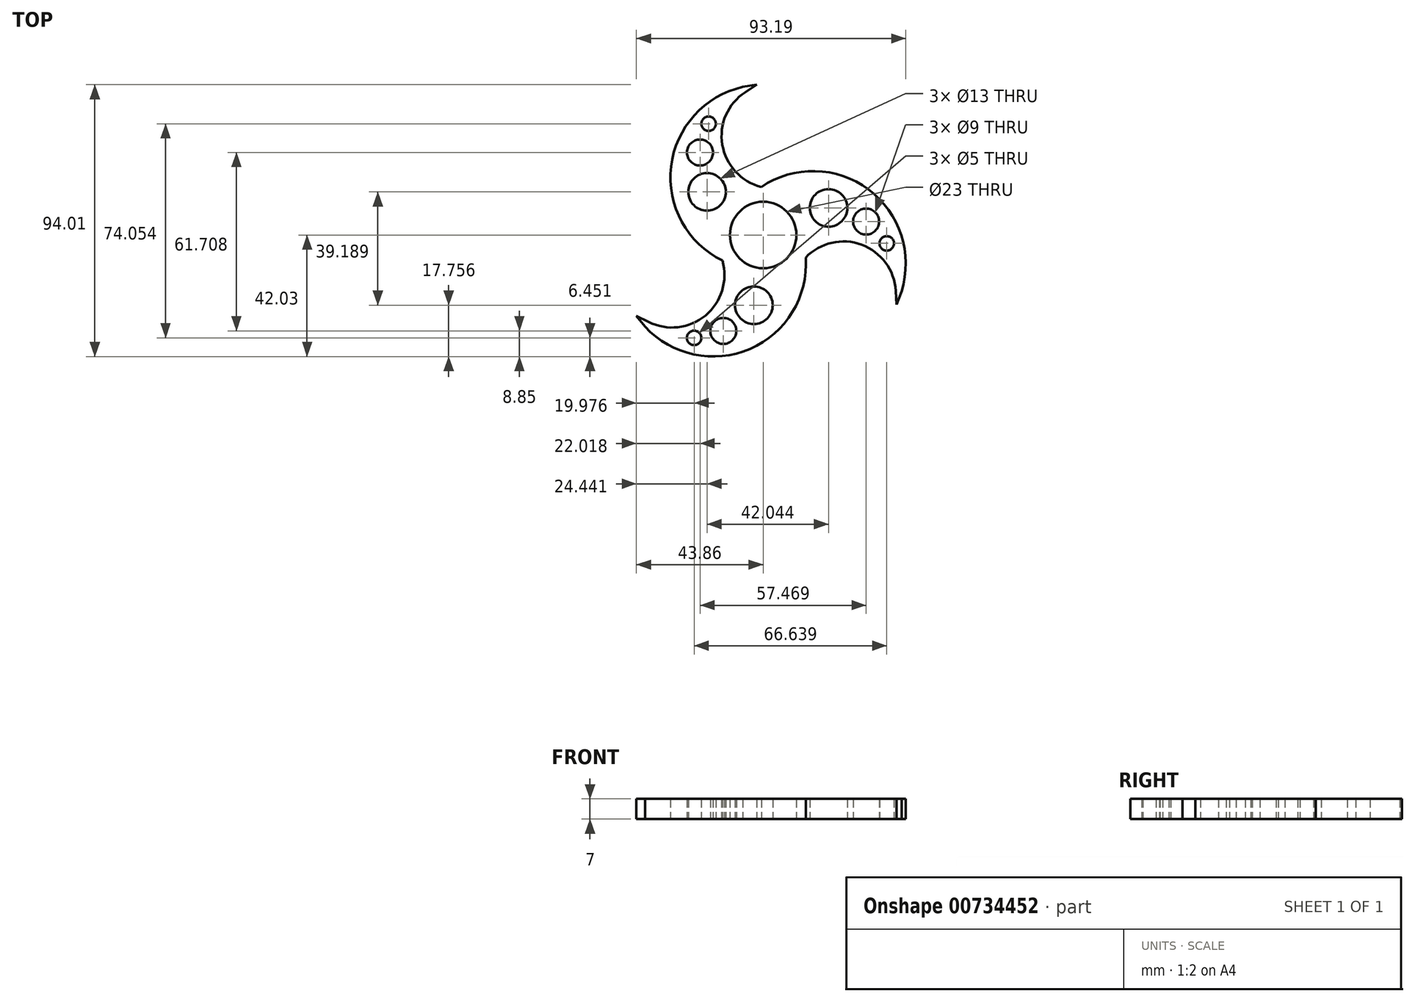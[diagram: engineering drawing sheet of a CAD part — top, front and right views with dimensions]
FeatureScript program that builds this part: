
annotation { "Feature Type Name" : "Feature", "Feature Type Description" : "" }
export const myFeature = defineFeature(function(context is Context, id is Id, definition is map)
    precondition{}
    {
        {
            var Q0;
            Q0=qCreatedBy(makeId("Top.planeOp"),FACE);
            var sketch = newSketch(context, id + "F0", { "sketchPlane" : qUnion([Q0])});
            skCircle(sketch, "E0", {"center": v(0, 0) * mm, "radius": 4 * mm});
            skCircle(sketch, "E1.0", {"center": v(0, 0) * mm, "radius": 16.48 * mm});
            skLineSegment(sketch, "E2", {"start": v(-13.8, -9.01) * mm, "end": v(0, 0) * mm});
            skLineSegment(sketch, "E3", {"start": v(0, 16.48) * mm, "end": v(0, 0) * mm});
            skPoint(sketch, "E4.trimOffspring.end.orphan", {"position": v(0, 16.48) * mm});
            skArc(sketch, "E5", {"start": v(-7.08, 51.2) * mm, "mid": v(-31.87, 23.5) * mm, "end": v(-13.8, -9.01) * mm});
            skArc(sketch, "E6", {"start": v(-6.22, 49.4) * mm, "mid": v(-14.07, 30.87) * mm, "end": v(0, 16.48) * mm});
            skPoint(sketch, "E7.orphan", {"position": v(0, 52) * mm});
            skCircle(sketch, "E8", {"center": v(0, 0) * mm, "radius": 11.5 * mm});
            skLineSegment(sketch, "E9", {"start": v(-6.22, 49.4) * mm, "end": v(-2.3, 51.98) * mm});
            skLineSegment(sketch, "E10", {"start": v(-2.3, 51.98) * mm, "end": v(-7.08, 51.2) * mm});
            skSolve(sketch);
        }
        {
            var Q0;
            {var subQ4=sQuery(id+"F0.wireOp",EDGE,"E5");Q0=makeQuery(id+"F0.imprint","IMPRINT",FACE,{"disambiguationData":[TD([[makeQuery(id+"F0.imprint","IMPRINT",EDGE,{"derivedFrom":subQ4}),1.0]])]});}
            var Q1;
            {var subQ0=sQuery(id+"F0.wireOp",EDGE,"E2");var subQ1=sQuery(id+"F0.wireOp",EDGE,"5BbXJLAx-Ili3-r6eS-Mn3f-kefYyYzVXHiO");var subQ2=makeQuery(id+"F0.imprint","INTERSECT",VERTEX,{"derivedFrom":[subQ1,subQ0]});Q1=makeQuery(id+"F0.imprint","IMPRINT",FACE,{"disambiguationData":[TD([[makeQuery(id+"F0.imprint","IMPRINT",EDGE,{"disambiguationData":[TD([[subQ2,1.0]])],"derivedFrom":subQ1}),-1.0]])]});}
            extrude(context, id + "F1", {"entities" : qUnion([Q0, Q1]), "depth" : 7 * mm, "offsetDistance" : 25 * mm});
        }
        {
            var Q0;
            Q0=qCreatedBy(makeId("Top.planeOp"),FACE);
            var sketch = newSketch(context, id + "F2", { "sketchPlane" : qUnion([Q0])});
            skCircle(sketch, "E11", {"center": v(-18.87, 38.47) * mm, "radius": 2.5 * mm});
            skArc(sketch, "E12", {"start": v(0, 52) * mm, "mid": v(-20.64, 34.32) * mm, "end": v(-14.5, 7.85) * mm});
            skCircle(sketch, "E13", {"center": v(-21.84, 28.53) * mm, "radius": 4.5 * mm});
            skCircle(sketch, "E14", {"center": v(-19.42, 14.91) * mm, "radius": 6.5 * mm});
            skSolve(sketch);
        }
        {
            var Q0;
            Q0=qCreatedBy(makeId("Right.planeOp"),FACE);
            var sketch = newSketch(context, id + "F3", { "sketchPlane" : qUnion([Q0])});
            skLineSegment(sketch, "E15", {"start": v(0, 29.24) * mm, "end": v(0, -32.64) * mm, "construction": true});
            skSolve(sketch);
        }
        {
            var Q0;
            Q0=qSketchRegion(id+"F2",true);
            extrude(context, id + "F4", {"entities" : qUnion([Q0]), "operationType" : NewBodyOperationType.REMOVE, "oppositeDirection" : true, "depth" : 25 * mm});
        }
        {
            var Q0;
            Q0=qSketchRegion(id+"F2",true);
            extrude(context, id + "F5", {"entities" : qUnion([Q0]), "operationType" : NewBodyOperationType.REMOVE, "oppositeDirection" : true, "depth" : 25 * mm});
        }
        {
            var Q0;
            Q0=qSketchRegion(id+"F2",true);
            extrude(context, id + "F6", {"entities" : qUnion([Q0]), "operationType" : NewBodyOperationType.REMOVE, "depth" : 25 * mm});
        }
        {
            var Q0;
            Q0=makeQuery(id+"F1.opExtrude","SWEPT_BODY",BODY,{"disambiguationData":[OSD([sQuery(id+"F0.wireOp",EDGE,"E1.0"),sQuery(id+"F0.wireOp",EDGE,"E2"),sQuery(id+"F0.wireOp",EDGE,"E5"),sQuery(id+"F0.wireOp",EDGE,"E6")])]});
            var Q1;
            Q1=sQuery(id+"F3.wireOp",EDGE,"E15");
            circularPattern(context, id + "F7", {"entities" : qUnion([Q0]), "axis" : qUnion([Q1]), "angle" : 360 * degree, "instanceCount" : 3, "equalSpace" : true});
        }
        {
            var Q0;
            {var subQ0=sQuery(id+"F0.wireOp",EDGE,"E2");var subQ5=sQuery(id+"F0.wireOp",EDGE,"E8");var subQ6=makeQuery(id+"F0.imprint","INTERSECT",VERTEX,{"derivedFrom":[subQ0,subQ5]});Q0=makeQuery(id+"F0.imprint","IMPRINT",FACE,{"disambiguationData":[TD([[makeQuery(id+"F0.imprint","IMPRINT",EDGE,{"disambiguationData":[TD([[subQ6,-1.0]])],"derivedFrom":subQ5}),-1.0]])]});}
            var Q1;
            {var subQ0=sQuery(id+"F0.wireOp",EDGE,"E2");var subQ5=sQuery(id+"F0.wireOp",EDGE,"E8");var subQ7=makeQuery(id+"F0.imprint","INTERSECT",VERTEX,{"derivedFrom":[subQ0,subQ5]});Q1=makeQuery(id+"F0.imprint","IMPRINT",FACE,{"disambiguationData":[TD([[makeQuery(id+"F0.imprint","IMPRINT",EDGE,{"disambiguationData":[TD([[subQ7,1.0]])],"derivedFrom":subQ5}),-1.0]])]});}
            extrude(context, id + "F8", {"entities" : qUnion([Q0, Q1]), "operationType" : NewBodyOperationType.ADD, "depth" : 7 * mm, "offsetDistance" : 25 * mm});
        }
    });
